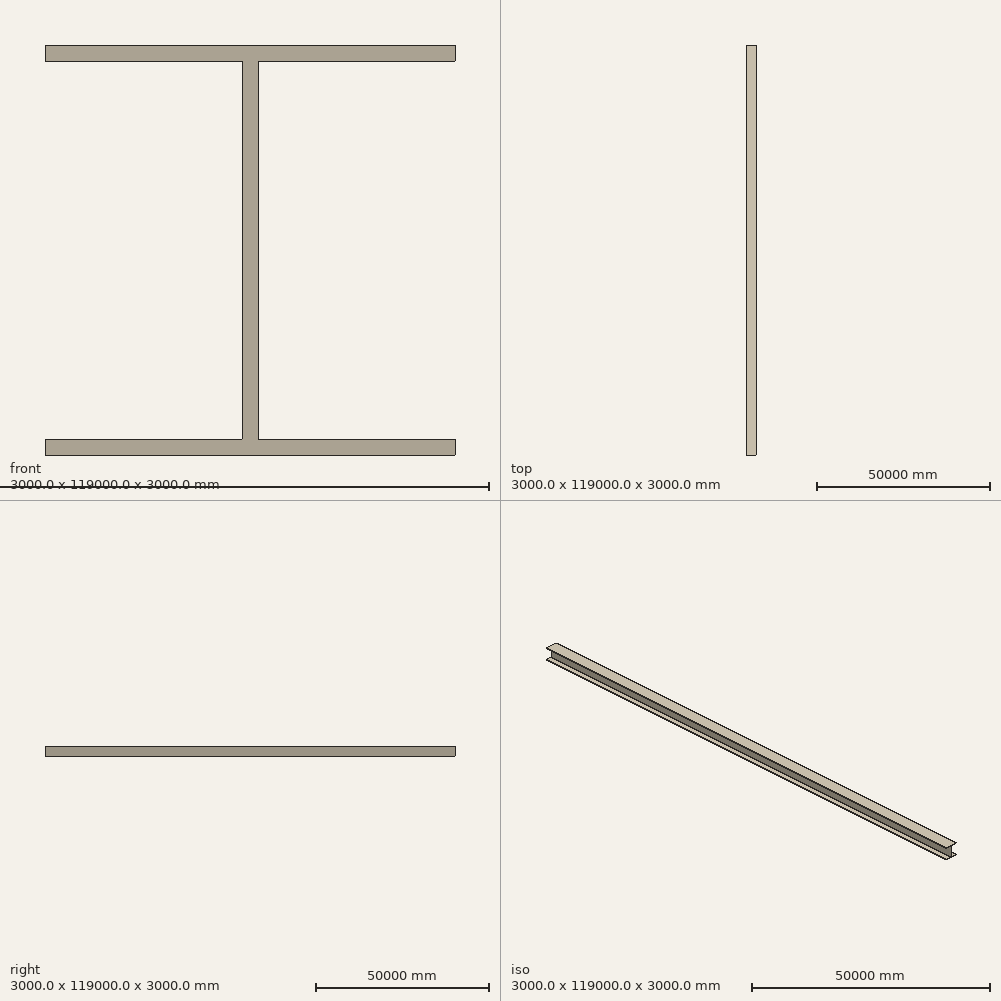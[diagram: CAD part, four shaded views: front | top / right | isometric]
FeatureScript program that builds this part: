
annotation { "Feature Type Name" : "Feature", "Feature Type Description" : "" }
export const myFeature = defineFeature(function(context is Context, id is Id, definition is map)
    precondition{}
    {
        {
            var Q0;
            Q0=qCreatedBy(makeId("Front.planeOp"),FACE);
            var sketch = newSketch(context, id + "F0", { "sketchPlane" : qUnion([Q0])});
            skLineSegment(sketch, "E0", {"start": v(0, 3000) * mm, "end": v(-1500, 3000) * mm});
            skLineSegment(sketch, "E1", {"start": v(-1500, 3000) * mm, "end": v(-1500, 2880) * mm});
            skLineSegment(sketch, "E2", {"start": v(-1500, 2880) * mm, "end": v(-60, 2880) * mm});
            skLineSegment(sketch, "E3", {"start": v(-60, 2880) * mm, "end": v(-60, 120) * mm});
            skLineSegment(sketch, "E4", {"start": v(-60, 120) * mm, "end": v(-1500, 120) * mm});
            skLineSegment(sketch, "E5", {"start": v(-1500, 120) * mm, "end": v(-1500, 0) * mm});
            skLineSegment(sketch, "E6", {"start": v(-1500, 0) * mm, "end": v(0, 0) * mm});
            skLineSegment(sketch, "E7.MirrorCS", {"start": v(1500, 3000) * mm, "end": v(1500, 2880) * mm});
            skLineSegment(sketch, "E8.MirrorCS", {"start": v(1500, 120) * mm, "end": v(1500, 0) * mm});
            skLineSegment(sketch, "E9.MirrorCS", {"start": v(1500, 0) * mm, "end": v(0, 0) * mm});
            skLineSegment(sketch, "E10.MirrorCS", {"start": v(60, 2880) * mm, "end": v(60, 120) * mm});
            skLineSegment(sketch, "E11.MirrorCS", {"start": v(0, 3000) * mm, "end": v(1500, 3000) * mm});
            skLineSegment(sketch, "E12.MirrorCS", {"start": v(1500, 2880) * mm, "end": v(60, 2880) * mm});
            skLineSegment(sketch, "E13.MirrorCS", {"start": v(60, 120) * mm, "end": v(1500, 120) * mm});
            skSolve(sketch);
        }
        {
            var Q0;
            Q0 = qSketchRegion(id + "F0", true);
            extrude(context, id + "F1", {"entities" : qUnion([Q0]), "depth" : 119000 * mm, "offsetDistance" : 25 * mm});
        }
    });
